# Revit family: Bright 5.F
name_source: partatom
category: Lighting Fixtures
revit_build: Autodesk Revit 2017 (Build: 20170419_0315(x64)
units: mm (PartAtom-declared; Revit-internal decimal feet)

## family parameters
Cut with Voids When Loaded = Yes
Host = Face
Light Source = Yes
Part Type = Normal
Room Calculation Point = Yes
Round Connector Dimension = Use Diameter
Shared = No

## types (16) — shared parameters
Apparent Load = 0 VA
Body = L&L_Anodized aluminium
CRI = 90 (also available: CRI 80 - ref. URL Technical sheet)
Code = -
Color Filter = 16777215
Control system = -
Cutout dimensions = diam. 125 mm
Default Elevation = 1219 mm
Delivered lumen output = 821 lm (3000K, 12°, 14W, CRI 80), 759 lm (3000K, 12°, 14W, CRI 90), 1208 lm (3000K, 12°, 19W, CRI 80), 1117 lm (3000K, 12°, 19W, CRI 90)
Description = recessed for outdoor applications
Dimming Lamp Color Temperature Shift = <None>
Emit from Line Length = 610 mm
Energy efficiency class = A A+ A++
Features = 67°x11° optics adjustable through 360° using the magnet provided
Geometry = Bright 5.F_mod
Height Void = 80 mm  [stored 0.262467 ft]
Height mm = 90 mm  [stored 0.295276 ft]
IP = IP68, IP69K
LED Colour = 3000K (also available: 2700K and 4000K - ref. URL Technical sheet)
Length mm = 148 mm  [stored 0.485564 ft]
Lens = L&L_Tempered extra-clear glass
Lumen output at source = 1663 lm (3000K, 19W, CRI 80), 1538 lm (3000K, 19W, CRI 90), 1131 lm (3000K, 14W, CRI 80), 1046 lm (3000K, 14W, CRI 90)
Manufacturer = L&L Luce&Light
Material = body in anodized aluminium, trim in AISI 316L stainless steel, screen in tempered, serigraphed-grey and transparent extra-clear glass
Model = Bright 5.F
Mounting = recessed (ceiling, wall, floor)
No. and type of led = 3 high-intensity power LEDs, 3-step MacAdam, 50 000h L95 B10 (Ta 25°C)
Notes = -
Power Supply = L&L_Steel inox AISI 316L
Power cables = includes 1,50 m neoprene cable, H05RN-F 2x0,75/0,75 Ø6,3 mm
Power supply = 24Vdc
Power supply unit = not included
Radius Void = 50 mm  [stored 0.164042 ft]
Tilt Angle = 90.00°
Tiltable = -
Trim = L&L_Steel inox AISI 316L
URL = https://www.lucelight.it
URL Accessories and power supply units = https://www.lucelight.it
URL Catalogue = https://www.lucelight.it
URL DXF = https://www.lucelight.it
URL Description = https://www.lucelight.it
URL General code = https://www.lucelight.it
URL IES Photometric file = https://www.lucelight.it
URL Image = https://www.lucelight.it
URL Technical sheet = https://www.lucelight.it
Voltage = 24 V
Weight kg = 1.35 kg
Width mm = 148 mm  [stored 0.485564 ft]
Wiring = parallel

## per-type parameters (varying)
| type | Apparent Load Phase 1 | Optics | Photometric Web File | Power |
| Bright 5.F K 56° (3000K 14W 24Vdc) | 14 W | 56° | BRIGHT 5.F K 56° [3000K 14W 24Vdc].IES | 14W |
| Bright 5.F L 35° (3000K 14W 24Vdc) | 14 W | 35° | BRIGHT 5.F L 35° [3000K 14W 24Vdc].IES | 14W |
| Bright 5.F M 31° (3000K 14W 24Vdc) | 14 W | 31° | BRIGHT 5.F M 31° [3000K 14W 24Vdc].IES | 14W |
| Bright 5.F T 12° (3000K 14W 24Vdc) | 14 W | 12° | BRIGHT 5.F T 12° [3000K 14W 24Vdc].IES | 14W |
| Bright 5.F S 18° (3000K 14W 24Vdc) | 14 W | 18° | BRIGHT 5.F S 18° [3000K 14W 24Vdc].IES | 14W |
| Bright 5.F V 10° (3000K 14W 24Vdc) | 14 W | 10° | BRIGHT 5.F V 10° [3000K 14W 24Vdc].IES | 14W |
| Bright 5.F X 67°x11° (3000K 14W 24Vdc) | 14 W | 67°x11° adjustable through 360° | BRIGHT 5.F X 67°x11° magnet [3000K 14W 24Vdc].IES | 14W |
| Bright 5.F W 15°x47° (3000K 14W 24Vdc) | 14 W | 15°x47° | BRIGHT 5.F W 15°x47° [3000K 14W 24Vdc].IES | 14W |
| Bright 5.F K 56° (3000K 19W 24Vdc) | 19 W | 56° | BRIGHT 5.F K 56° [3000K 19W 24Vdc].IES | 19W |
| Bright 5.F L 35° (3000K 19W 24Vdc) | 19 W | 35° | BRIGHT 5.F L 35° [3000K 19W 24Vdc].IES | 19W |
| Bright 5.F M 31° (3000K 19W 24Vdc) | 19 W | 31° | BRIGHT 5.F M 31° [3000K 19W 24Vdc].IES | 19W |
| Bright 5.F S 18° (3000K 19W 24Vdc) | 19 W | 18° | BRIGHT 5.F S 18° [3000K 19W 24Vdc].IES | 19W |
| Bright 5.F T 12° (3000K 19W 24Vdc) | 19 W | 12° | BRIGHT 5.F T 12° [3000K 19W 24Vdc].IES | 19W |
| Bright 5.F V 10° (3000K 19W 24Vdc) | 19 W | 10° | BRIGHT 5.F V 10° [3000K 19W 24Vdc].IES | 19W |
| Bright 5.F X 67°x11° (3000K 19W 24Vdc) | 19 W | 67°x11° adjustable through 360° | BRIGHT 5.F X 67°x11° magnet [3000K 19W 24Vdc].IES | 19W |
| Bright 5.F W 15°x47° (3000K 19W 24Vdc) | 19 W | 15°x47° | BRIGHT 5.F W 15°x47° [3000K 19W 24Vdc].IES | 19W |

note: [stored X ft] marks values corroborated as IEEE doubles in the binary element streams (Revit-internal decimal feet)

## geometry (parser evidence)
native form markers: Blend x2, Sweep x9
no freeform markers — native parametric forms only
